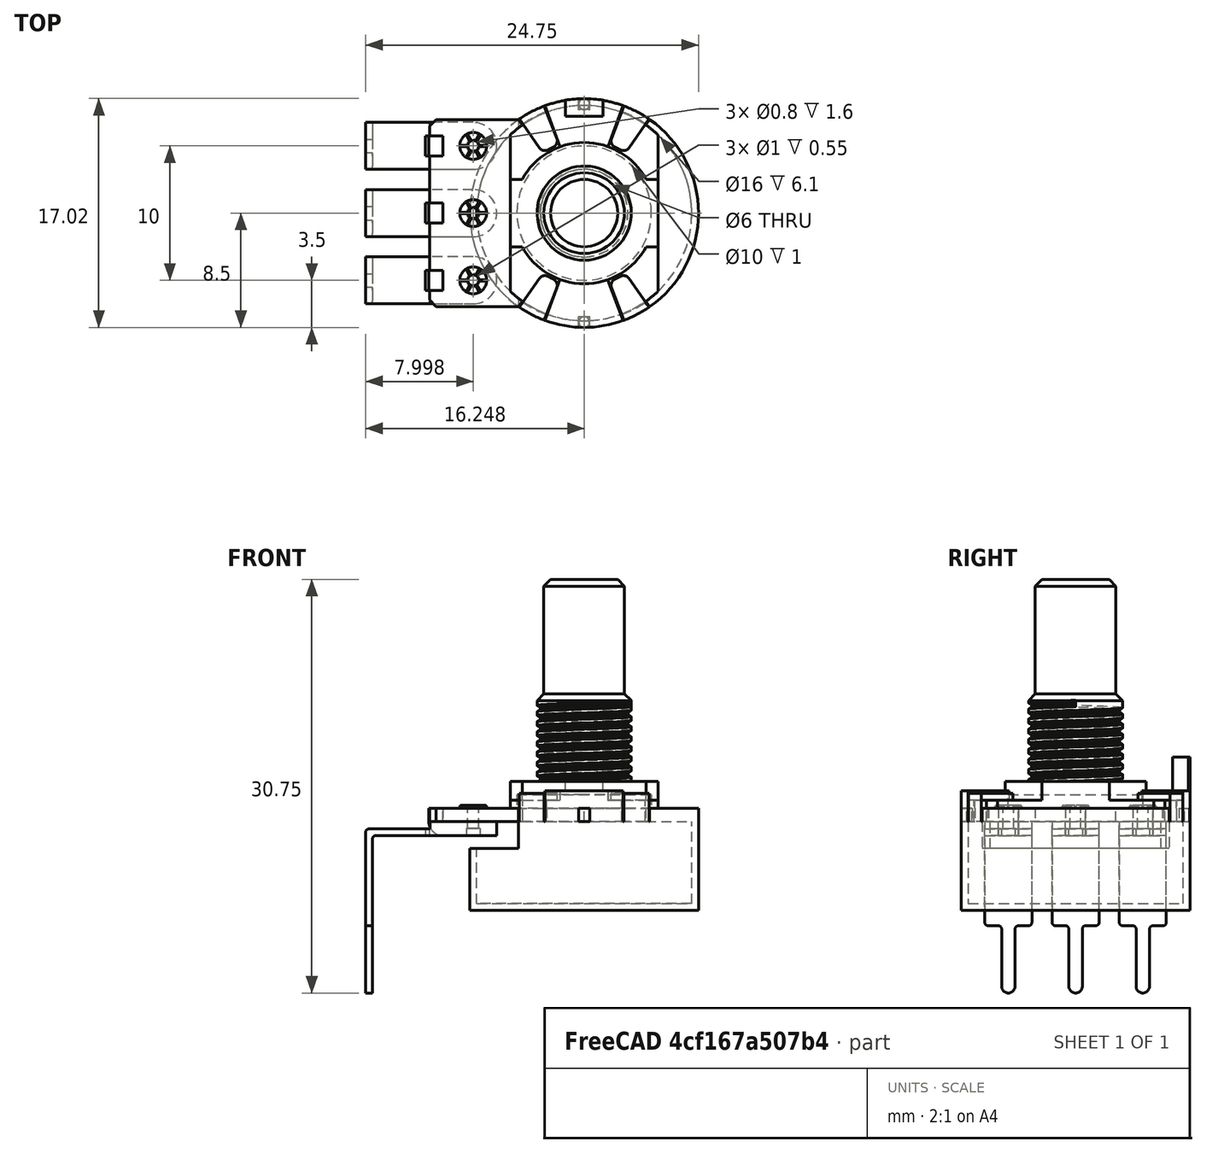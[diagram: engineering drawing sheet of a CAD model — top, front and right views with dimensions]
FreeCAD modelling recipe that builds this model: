
FCSTD DOCUMENT  (FreeCAD 0.19R17089 +1543 (Git))
Label: #000-000 - Mu-Tron Phasor II - ASM3 Assembly
License: All rights reserved
LicenseURL: http://en.wikipedia.org/wiki/All_rights_reserved
objects: App::Link×12, App::FeaturePython×8, Part::FeaturePython×7, App::Part×3, Part::Feature×1
note: 7 computed .brp shape members not serialized (recipe doc carries the construction recipe); baked Part::Feature solids carry a one-line shape summary decoded from their .brp
EXTERNAL_REF file=#100-000 - Phasor PCB Assembly.FCStd obj=Board_3323
EXTERNAL_REF file=#200-000 - Photomodule PCB Assembly.FCStd obj=Board_9fc9
EXTERNAL_REF file=../../#700-000 - Enclosure/#700-000-A - Enclosure [1590DD, Portrait]/#700-000-A - Enclosure [1590DD, Portrait].FCStd obj=Part
EXTERNAL_REF file=../../#400-000 - Switching PCB Assembly/#400-000-A - Switching PCBA [DPDT, Latching]/#400-000-A - Switching PCBA [DPDT, Latching].FCStd obj=Board
EXTERNAL_REF file=../../#500-000 - Audio Jack PCB Assembly/#500-000-A1 [Input, Pads L]/#500-000-A1 - Audio Jack PCBA [Input, Pads L].FCStd obj=Board_8681
EXTERNAL_REF file=../../#500-000 - Audio Jack PCB Assembly/#500-000-A2 [Output, Pads R]/#510-000-A2 [Output, Pads R].FCStd obj=Board_5daf
EXTERNAL_REF file=../../#600-000 - Power Jack PCB Assembly/#600-000-A - Power Jack PCB [1614 09]/#610-000-S1C - Power Jack PCB [1614 09, Narrow, Minimal Protection].FCStd obj=Board_4eef
EXTERNAL_REF file=../../#800-000 - Finishing Materials/#800-XXX - Knob Synthie 2.FCStd obj=Part
EXTERNAL_REF file=../../#800-000 - Finishing Materials/#800-XXX - Knob Synthie 2.FCStd obj=Part001
EXTERNAL_REF file=../../#800-000 - Finishing Materials/#800-XXX - Knob Synthie 2.FCStd obj=Part002

FEATURE [App::Link] Link  label="#100-000 - Phasor PCBA"
  LinkPlacement = pos=(-9.095e-13,1.57356e-05,-38.7) rot=(0,0,1;0rad)
  LinkedObject = -> <external #100-000 - Phasor PCB Assembly.FCStd>#Board_3323
  Placement = pos=(-9.095e-13,1.57356e-05,-38.7) rot=(0,0,1;0rad)
FEATURE [App::Link] Link001  label="#200-000 - Photomodule PCBA"
  LinkPlacement = pos=(-13.0175,19.05,23.54) rot=(0,0,1;1.5708rad)
  LinkedObject = -> <external #200-000 - Photomodule PCB Assembly.FCStd>#Board_9fc9
  Placement = pos=(-13.0175,19.05,23.54) rot=(0,0,1;1.5708rad)
  expr: .Placement.Base.z = 4.1399999999999997 + 19.399999999999999
FEATURE [App::Link] Link002  label="#700-000 - Enclosure"
  LinkPlacement = pos=(0,-1.75238e-05,147) rot=(0,0,1;0rad)
  LinkedObject = -> <external ../../#700-000 - Enclosure/#700-000-A - Enclosure [1590DD, Portrait]/#700-000-A - Enclosure [1590DD, Portrait].FCStd>#Part
  Placement = pos=(0,-1.75238e-05,147) rot=(0,0,1;0rad)
FEATURE [App::Link] Link003  label="#400-000 - Switching PCBA"
  LinkPlacement = pos=(0,-60,17) rot=(0,0,1;0rad)
  LinkedObject = -> <external ../../#400-000 - Switching PCB Assembly/#400-000-A - Switching PCBA [DPDT, Latching]/#400-000-A - Switching PCBA [DPDT, Latching].FCStd>#Board
  Placement = pos=(0,-60,17) rot=(0,0,1;0rad)
FEATURE [App::Link] Link004  label="#500-000 - Input Jack PCBA"
  LinkPlacement = pos=(23.2,91.7,2.55) rot=(0,0,1;0rad)
  LinkedObject = -> <external ../../#500-000 - Audio Jack PCB Assembly/#500-000-A1 [Input, Pads L]/#500-000-A1 - Audio Jack PCBA [Input, Pads L].FCStd>#Board_8681
  Placement = pos=(23.2,91.7,2.55) rot=(0,0,1;0rad)
FEATURE [App::Link] Link005  label="#500-000 - Output Jack PCBA"
  LinkPlacement = pos=(-23.2,91.7,2.55) rot=(0,0,1;0rad)
  LinkedObject = -> <external ../../#500-000 - Audio Jack PCB Assembly/#500-000-A2 [Output, Pads R]/#510-000-A2 [Output, Pads R].FCStd>#Board_5daf
  Placement = pos=(-23.2,91.7,2.55) rot=(0,0,1;0rad)
FEATURE [App::Link] Link006  label="#600-000 - Power Jack PCBA"
  LinkPlacement = pos=(0.377903,85.317,9) rot=(0.57735,0.57735,0.57735;4.18879rad)
  LinkedObject = -> <external ../../#600-000 - Power Jack PCB Assembly/#600-000-A - Power Jack PCB [1614 09]/#610-000-S1C - Power Jack PCB [1614 09, Narrow, Minimal Protection].FCStd>#Board_4eef
  Placement = pos=(0.377903,85.317,9) rot=(0.57735,0.57735,0.57735;4.18879rad)
FEATURE [App::Link] Link007  label="#800-XXX - Knob Depth"
  LinkPlacement = pos=(37,-1.66893e-05,103) rot=(0,0,1;0rad)
  LinkedObject = -> <external ../../#800-000 - Finishing Materials/#800-XXX - Knob Synthie 2.FCStd>#Part
  Placement = pos=(37,-1.66893e-05,103) rot=(0,0,1;0rad)
FEATURE [App::Link] Link008  label="#800-XXX - Knob Rate"
  LinkPlacement = pos=(78,-2.0504e-05,94) rot=(0,0,1;0rad)
  LinkedObject = -> <external ../../#800-000 - Finishing Materials/#800-XXX - Knob Synthie 2.FCStd>#Part001
  Placement = pos=(78,-2.0504e-05,94) rot=(0,0,1;0rad)
FEATURE [App::Link] Link009  label="#800-XXX - Knob Feedback"
  LinkPlacement = pos=(-41,-4.17233e-06,76) rot=(0,0,1;0rad)
  LinkedObject = -> <external ../../#800-000 - Finishing Materials/#800-XXX - Knob Synthie 2.FCStd>#Part002
  Placement = pos=(-41,-4.17233e-06,76) rot=(0,0,1;0rad)
FEATURE [Part::Feature] Shape009  label=""RV55"_Alpha_RV16AF-41-15R-XXX_5DD3C757"
  Placement = pos=(43.4975,58.42,0) rot=(0,0,-1;1.5708rad)
  shape: bbox 24.75 x 17.02 x 30.75 mm, 459 faces (baked)
FEATURE [App::Link] _RV55__Alpha_RV16AF_41_15R_XXX_5DD3C757_ln_  label=""RV54"_Alpha_RV16AF-41-15R-XXX_5DC04847"
  LinkPlacement = pos=(0,58.42,0) rot=(0,0,1;1.5708rad)
  LinkedObject = -> Shape009
  Placement = pos=(0,58.42,0) rot=(0,0,1;1.5708rad)
FEATURE [App::Link] _RV55__Alpha_RV16AF_41_15R_XXX_5DD3C757_ln_001  label=""RV53"_Alpha_RV16AF-41-15R-XXX_5DF1A8EF"
  LinkPlacement = pos=(-43.4975,58.42,0) rot=(0,0,1;1.5708rad)
  LinkedObject = -> Shape009
  Placement = pos=(-43.4975,58.42,0) rot=(0,0,1;1.5708rad)
FEATURE [App::Part] Part  label="#110-XXX - Pot Feedback"
  Group = -> [_RV55__Alpha_RV16AF_41_15R_XXX_5DD3C757_ln_001]
  Origin = -> Origin
FEATURE [App::Part] Part001  label="#110-XXX - Pot Depth"
  Group = -> [_RV55__Alpha_RV16AF_41_15R_XXX_5DD3C757_ln_]
  Origin = -> Origin001
FEATURE [App::Part] Part002  label="#110-XXX - Pot Rate"
  Group = -> [Shape009]
  Origin = -> Origin002
FEATURE [Part::FeaturePython] Parts  # WARN: FeaturePython — macro-defined, semantics opaque (R4)
  Group = -> [Link,Part,Part001,Part002,Link001,Link003,Link004,Link005,Link006,Link002,Link009,Link007,Link008]
  GroupMode = 0
FEATURE [Part::FeaturePython] Assembly  # WARN: FeaturePython — macro-defined, semantics opaque (R4)
  AutoRelax = true
  BuildShape = 0
  Freeze = false
  Group = -> [Constraints,Elements,Parts]
  GroupMode = 1
  SolverType = 1
  Verbose = false
  _SolverType = 1
  _Version = 1
FEATURE [App::FeaturePython] Constraints  # WARN: FeaturePython — macro-defined, semantics opaque (R4)
  Group = -> [Constraint,Constraint001]
  GroupMode = 1
  _Version = 1
FEATURE [App::FeaturePython] Elements  # WARN: FeaturePython — macro-defined, semantics opaque (R4)
  Group = -> [Element,Element001,Element002,Element003,Element004]
  GroupMode = 1
FEATURE [Part::FeaturePython] Element  # link proxy (typed FeaturePython)
  Detach = false
  LinkTransform = true
  LinkedObject = -> Link [Board_Geoms_3323.Pcb_3323.Edge740]
  _Parent = -> Elements
FEATURE [Part::FeaturePython] Element001  # link proxy (typed FeaturePython)
  Detach = false
  LinkTransform = true
  LinkedObject = -> Link [Board_Geoms_3323.Pcb_3323.Edge551]
  _Parent = -> Elements
FEATURE [Part::FeaturePython] Element002  # link proxy (typed FeaturePython)
  Detach = false
  LinkTransform = true
  LinkedObject = -> Link001 [Step_Models_9fc9.Bot_9fc9.J2_Pin_Header_Straight_01x05_ShortPins005_cp_5DBF3AB1_ln_.Face28]
  _Parent = -> Elements
FEATURE [Part::FeaturePython] Element003  # link proxy (typed FeaturePython)
  Detach = false
  LinkTransform = true
  LinkedObject = -> Link001 [Step_Models_9fc9.Bot_9fc9.Shape001.Face140]
  _Parent = -> Elements
FEATURE [App::FeaturePython] Constraint  label="AxialAlignment"  # WARN: FeaturePython — macro-defined, semantics opaque (R4)
  Angle = 0
  AnglePitch = 0
  AngleRoll = 0
  ConstraintType = 4
  Disabled = false
  Group = -> [ElementLink,ElementLink001]
  GroupMode = 1
  LockAngle = false
  Multiply = false
  _ConstraintType = 36
  _Parent = -> Constraints
FEATURE [App::FeaturePython] ElementLink  label="Element"  # link proxy (typed FeaturePython)
  LinkTransform = true
  LinkedObject = -> Element
  _Parent = -> Constraint
FEATURE [App::FeaturePython] ElementLink001  label="Element002"  # link proxy (typed FeaturePython)
  LinkTransform = true
  LinkedObject = -> Element002
  _Parent = -> Constraint
FEATURE [App::FeaturePython] Constraint001  label="AxialAlignment001"  # WARN: FeaturePython — macro-defined, semantics opaque (R4)
  Angle = 0
  AnglePitch = 0
  AngleRoll = 0
  ConstraintType = 4
  Disabled = false
  Group = -> [ElementLink002,ElementLink003]
  GroupMode = 1
  LockAngle = false
  Multiply = false
  _ConstraintType = 36
  _Parent = -> Constraints
FEATURE [App::FeaturePython] ElementLink002  label="Element001"  # link proxy (typed FeaturePython)
  LinkTransform = true
  LinkedObject = -> Element001
  _Parent = -> Constraint001
FEATURE [App::FeaturePython] ElementLink003  label="Element003"  # link proxy (typed FeaturePython)
  LinkTransform = true
  LinkedObject = -> Element003
  _Parent = -> Constraint001
FEATURE [Part::FeaturePython] Element004  # link proxy (typed FeaturePython)
  Detach = false
  LinkTransform = true
  LinkedObject = -> Link [Board_Geoms_3323.Pcb_3323.Face678]
  _Parent = -> Elements
